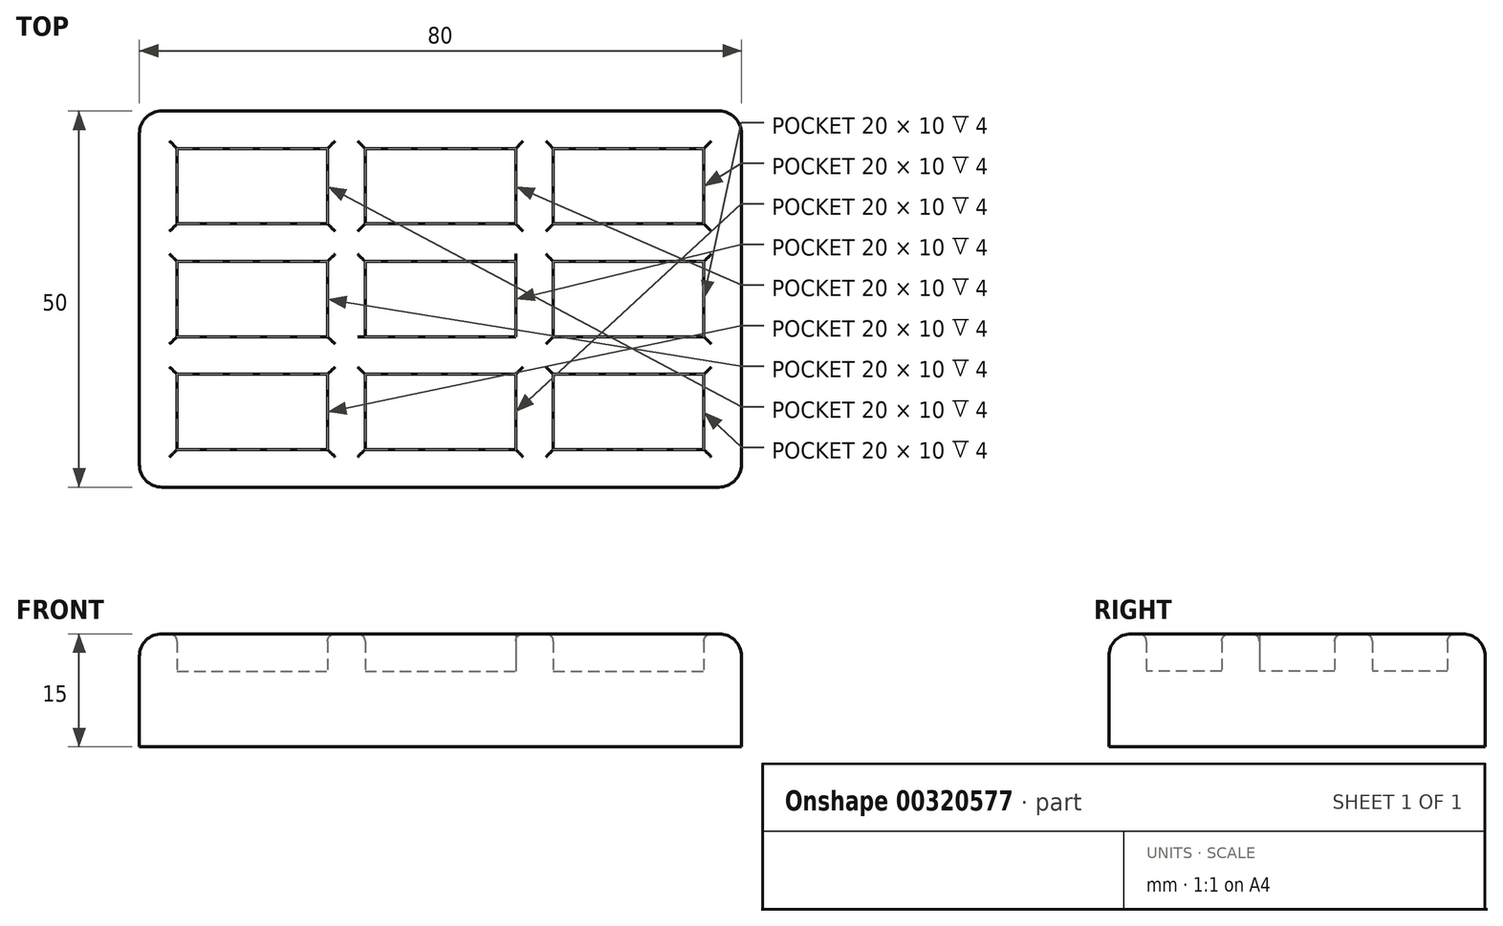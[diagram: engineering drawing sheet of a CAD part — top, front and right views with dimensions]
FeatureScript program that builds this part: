
annotation { "Feature Type Name" : "Feature", "Feature Type Description" : "" }
export const myFeature = defineFeature(function(context is Context, id is Id, definition is map)
    precondition{}
    {
        {
            var Q0;
            Q0=qCreatedBy(makeId("Top.planeOp"),FACE);
            var sketch = newSketch(context, id + "F0", { "sketchPlane" : qUnion([Q0])});
            skLineSegment(sketch, "E0.bottom", {"start": v(-40, 25) * mm, "end": v(40, 25) * mm});
            skLineSegment(sketch, "E0.top", {"start": v(-40, -25) * mm, "end": v(40, -25) * mm});
            skLineSegment(sketch, "E0.left", {"start": v(-40, 25) * mm, "end": v(-40, -25) * mm});
            skLineSegment(sketch, "E0.right", {"start": v(40, 25) * mm, "end": v(40, -25) * mm});
            skPoint(sketch, "E1", {"position": v(0, 25) * mm});
            skPoint(sketch, "E2", {"position": v(-40, 0) * mm});
            skLineSegment(sketch, "E3.bottom", {"start": v(-35, 20) * mm, "end": v(-15, 20) * mm});
            skLineSegment(sketch, "E3.top", {"start": v(-35, 10) * mm, "end": v(-15, 10) * mm});
            skLineSegment(sketch, "E3.left", {"start": v(-35, 20) * mm, "end": v(-35, 10) * mm});
            skLineSegment(sketch, "E3.right", {"start": v(-15, 20) * mm, "end": v(-15, 10) * mm});
            skLineSegment(sketch, "E4.0.1.0", {"start": v(-35, -5) * mm, "end": v(-15, -5) * mm});
            skLineSegment(sketch, "E4.0.1.1", {"start": v(-15, 5) * mm, "end": v(-15, -5) * mm});
            skLineSegment(sketch, "E4.0.1.2", {"start": v(-35, 5) * mm, "end": v(-15, 5) * mm});
            skLineSegment(sketch, "E4.0.1.3", {"start": v(-35, 5) * mm, "end": v(-35, -5) * mm});
            skLineSegment(sketch, "E4.0.2.0", {"start": v(-35, -20) * mm, "end": v(-15, -20) * mm});
            skLineSegment(sketch, "E4.0.2.1", {"start": v(-15, -10) * mm, "end": v(-15, -20) * mm});
            skLineSegment(sketch, "E4.0.2.2", {"start": v(-35, -10) * mm, "end": v(-15, -10) * mm});
            skLineSegment(sketch, "E4.0.2.3", {"start": v(-35, -10) * mm, "end": v(-35, -20) * mm});
            skLineSegment(sketch, "E4.1.0.0", {"start": v(-10, 10) * mm, "end": v(10, 10) * mm});
            skLineSegment(sketch, "E4.1.0.1", {"start": v(10, 20) * mm, "end": v(10, 10) * mm});
            skLineSegment(sketch, "E4.1.0.2", {"start": v(-10, 20) * mm, "end": v(10, 20) * mm});
            skLineSegment(sketch, "E4.1.0.3", {"start": v(-10, 20) * mm, "end": v(-10, 10) * mm});
            skLineSegment(sketch, "E4.1.1.0", {"start": v(-10, -5) * mm, "end": v(10, -5) * mm});
            skLineSegment(sketch, "E4.1.1.1", {"start": v(10, 5) * mm, "end": v(10, -5) * mm});
            skLineSegment(sketch, "E4.1.1.2", {"start": v(-10, 5) * mm, "end": v(10, 5) * mm});
            skLineSegment(sketch, "E4.1.1.3", {"start": v(-10, 5) * mm, "end": v(-10, -5) * mm});
            skLineSegment(sketch, "E4.1.2.0", {"start": v(-10, -20) * mm, "end": v(10, -20) * mm});
            skLineSegment(sketch, "E4.1.2.1", {"start": v(10, -10) * mm, "end": v(10, -20) * mm});
            skLineSegment(sketch, "E4.1.2.2", {"start": v(-10, -10) * mm, "end": v(10, -10) * mm});
            skLineSegment(sketch, "E4.1.2.3", {"start": v(-10, -10) * mm, "end": v(-10, -20) * mm});
            skLineSegment(sketch, "E4.2.0.0", {"start": v(15, 10) * mm, "end": v(35, 10) * mm});
            skLineSegment(sketch, "E4.2.0.1", {"start": v(35, 20) * mm, "end": v(35, 10) * mm});
            skLineSegment(sketch, "E4.2.0.2", {"start": v(15, 20) * mm, "end": v(35, 20) * mm});
            skLineSegment(sketch, "E4.2.0.3", {"start": v(15, 20) * mm, "end": v(15, 10) * mm});
            skLineSegment(sketch, "E4.2.1.0", {"start": v(15, -5) * mm, "end": v(35, -5) * mm});
            skLineSegment(sketch, "E4.2.1.1", {"start": v(35, 5) * mm, "end": v(35, -5) * mm});
            skLineSegment(sketch, "E4.2.1.2", {"start": v(15, 5) * mm, "end": v(35, 5) * mm});
            skLineSegment(sketch, "E4.2.1.3", {"start": v(15, 5) * mm, "end": v(15, -5) * mm});
            skLineSegment(sketch, "E4.2.2.0", {"start": v(15, -20) * mm, "end": v(35, -20) * mm});
            skLineSegment(sketch, "E4.2.2.1", {"start": v(35, -10) * mm, "end": v(35, -20) * mm});
            skLineSegment(sketch, "E4.2.2.2", {"start": v(15, -10) * mm, "end": v(35, -10) * mm});
            skLineSegment(sketch, "E4.2.2.3", {"start": v(15, -10) * mm, "end": v(15, -20) * mm});
            skLineSegment(sketch, "E4.direction1", {"start": v(-35, 10) * mm, "end": v(-10, 10) * mm, "construction": true});
            skLineSegment(sketch, "E4.direction2", {"start": v(-35, 10) * mm, "end": v(-35, -5) * mm, "construction": true});
            skSolve(sketch);
        }
        {
            var Q0;
            Q0=makeQuery(id+"F0.imprint","IMPRINT",FACE,{"disambiguationData":[TD([[makeQuery(id+"F0.imprint","IMPRINT",EDGE,{"derivedFrom":sQuery(id+"F0.wireOp",EDGE,"E0.bottom")}),-1.0]])]});
            var Q1;
            Q1=makeQuery(id+"F0.imprint","IMPRINT",FACE,{"disambiguationData":[TD([[makeQuery(id+"F0.imprint","IMPRINT",EDGE,{"derivedFrom":sQuery(id+"F0.wireOp",EDGE,"E3.bottom")}),-1.0]])]});
            var Q2;
            Q2=makeQuery(id+"F0.imprint","IMPRINT",FACE,{"disambiguationData":[TD([[makeQuery(id+"F0.imprint","IMPRINT",EDGE,{"derivedFrom":sQuery(id+"F0.wireOp",EDGE,"E4.1.0.0")}),1.0]])]});
            var Q3;
            Q3=makeQuery(id+"F0.imprint","IMPRINT",FACE,{"disambiguationData":[TD([[makeQuery(id+"F0.imprint","IMPRINT",EDGE,{"derivedFrom":sQuery(id+"F0.wireOp",EDGE,"E4.2.0.0")}),1.0]])]});
            var Q4;
            Q4=makeQuery(id+"F0.imprint","IMPRINT",FACE,{"disambiguationData":[TD([[makeQuery(id+"F0.imprint","IMPRINT",EDGE,{"derivedFrom":sQuery(id+"F0.wireOp",EDGE,"E4.2.1.0")}),1.0]])]});
            var Q5;
            Q5=makeQuery(id+"F0.imprint","IMPRINT",FACE,{"disambiguationData":[TD([[makeQuery(id+"F0.imprint","IMPRINT",EDGE,{"derivedFrom":sQuery(id+"F0.wireOp",EDGE,"E4.1.1.0")}),1.0]])]});
            var Q6;
            Q6=makeQuery(id+"F0.imprint","IMPRINT",FACE,{"disambiguationData":[TD([[makeQuery(id+"F0.imprint","IMPRINT",EDGE,{"derivedFrom":sQuery(id+"F0.wireOp",EDGE,"E4.0.1.0")}),1.0]])]});
            var Q7;
            Q7=makeQuery(id+"F0.imprint","IMPRINT",FACE,{"disambiguationData":[TD([[makeQuery(id+"F0.imprint","IMPRINT",EDGE,{"derivedFrom":sQuery(id+"F0.wireOp",EDGE,"E4.0.2.0")}),1.0]])]});
            var Q8;
            Q8=makeQuery(id+"F0.imprint","IMPRINT",FACE,{"disambiguationData":[TD([[makeQuery(id+"F0.imprint","IMPRINT",EDGE,{"derivedFrom":sQuery(id+"F0.wireOp",EDGE,"E4.1.2.0")}),1.0]])]});
            var Q9;
            Q9=makeQuery(id+"F0.imprint","IMPRINT",FACE,{"disambiguationData":[TD([[makeQuery(id+"F0.imprint","IMPRINT",EDGE,{"derivedFrom":sQuery(id+"F0.wireOp",EDGE,"E4.2.2.0")}),1.0]])]});
            extrude(context, id + "F1", {"entities" : qUnion([Q0, Q1, Q2, Q3, Q4, Q5, Q6, Q7, Q8, Q9]), "oppositeDirection" : true, "depth" : 10 * mm});
        }
        {
            var Q0;
            Q0 = qSketchRegion(id + "F0", true);
            extrude(context, id + "F2", {"entities" : qUnion([Q0]), "operationType" : NewBodyOperationType.ADD, "depth" : 5 * mm});
        }
        {
            var Q0;
            {var subQ0=sQuery(id+"F0.wireOp",EDGE,"E0.left");var subQ1=sQuery(id+"F0.wireOp",EDGE,"E0.top");Q0=makeQuery(id+"F2.boolean.opBoolean","MERGE",EDGE,{"derivedFrom":[makeQuery(id+"F1.opExtrude","SWEPT_EDGE",EDGE,{"disambiguationData":[OSD([subQ1,subQ0])]}),makeQuery(id+"F2.opExtrude","SWEPT_EDGE",EDGE,{"disambiguationData":[OSD([subQ1,subQ0])]})]});}
            var Q1;
            {var subQ0=sQuery(id+"F0.wireOp",EDGE,"E0.right");var subQ1=sQuery(id+"F0.wireOp",EDGE,"E0.top");Q1=makeQuery(id+"F2.boolean.opBoolean","MERGE",EDGE,{"derivedFrom":[makeQuery(id+"F1.opExtrude","SWEPT_EDGE",EDGE,{"disambiguationData":[OSD([subQ1,subQ0])]}),makeQuery(id+"F2.opExtrude","SWEPT_EDGE",EDGE,{"disambiguationData":[OSD([subQ1,subQ0])]})]});}
            var Q2;
            Q2=makeQuery(id+"F2.opExtrude","CAP_EDGE",EDGE,{"disambiguationData":[OSD([sQuery(id+"F0.wireOp",EDGE,"E0.top")])],"isStart":false});
            var Q3;
            Q3=makeQuery(id+"F2.opExtrude","CAP_EDGE",EDGE,{"disambiguationData":[OSD([sQuery(id+"F0.wireOp",EDGE,"E0.left")])],"isStart":false});
            var Q4;
            Q4=makeQuery(id+"F2.opExtrude","CAP_EDGE",EDGE,{"disambiguationData":[OSD([sQuery(id+"F0.wireOp",EDGE,"E0.right")])],"isStart":false});
            var Q5;
            {var subQ0=sQuery(id+"F0.wireOp",EDGE,"E0.right");var subQ1=sQuery(id+"F0.wireOp",EDGE,"E0.bottom");Q5=makeQuery(id+"F2.boolean.opBoolean","MERGE",EDGE,{"derivedFrom":[makeQuery(id+"F1.opExtrude","SWEPT_EDGE",EDGE,{"disambiguationData":[OSD([subQ1,subQ0])]}),makeQuery(id+"F2.opExtrude","SWEPT_EDGE",EDGE,{"disambiguationData":[OSD([subQ1,subQ0])]})]});}
            var Q6;
            Q6=makeQuery(id+"F2.opExtrude","CAP_EDGE",EDGE,{"disambiguationData":[OSD([sQuery(id+"F0.wireOp",EDGE,"E0.bottom")])],"isStart":false});
            var Q7;
            {var subQ0=sQuery(id+"F0.wireOp",EDGE,"E0.left");var subQ1=sQuery(id+"F0.wireOp",EDGE,"E0.bottom");Q7=makeQuery(id+"F2.boolean.opBoolean","MERGE",EDGE,{"derivedFrom":[makeQuery(id+"F1.opExtrude","SWEPT_EDGE",EDGE,{"disambiguationData":[OSD([subQ1,subQ0])]}),makeQuery(id+"F2.opExtrude","SWEPT_EDGE",EDGE,{"disambiguationData":[OSD([subQ1,subQ0])]})]});}
            fillet(context, id + "F3", {"entities" : qUnion([Q0, Q1, Q2, Q3, Q4, Q5, Q6, Q7]), "radius" : 3 * mm, "tangentPropagation" : true, "allowEdgeOverflow" : false});
        }
        {
            var Q0;
            Q0=makeQuery(id+"F2.opExtrude","CAP_EDGE",EDGE,{"disambiguationData":[OSD([sQuery(id+"F0.wireOp",EDGE,"E4.0.2.1")])],"isStart":false});
            var Q1;
            Q1=makeQuery(id+"F2.opExtrude","CAP_EDGE",EDGE,{"disambiguationData":[OSD([sQuery(id+"F0.wireOp",EDGE,"E4.0.2.2")])],"isStart":false});
            var Q2;
            Q2=makeQuery(id+"F2.opExtrude","CAP_EDGE",EDGE,{"disambiguationData":[OSD([sQuery(id+"F0.wireOp",EDGE,"E4.0.2.3")])],"isStart":false});
            var Q3;
            Q3=makeQuery(id+"F2.opExtrude","CAP_EDGE",EDGE,{"disambiguationData":[OSD([sQuery(id+"F0.wireOp",EDGE,"E4.0.2.0")])],"isStart":false});
            var Q4;
            Q4=makeQuery(id+"F2.opExtrude","CAP_EDGE",EDGE,{"disambiguationData":[OSD([sQuery(id+"F0.wireOp",EDGE,"E4.0.1.1")])],"isStart":false});
            var Q5;
            Q5=makeQuery(id+"F2.opExtrude","CAP_EDGE",EDGE,{"disambiguationData":[OSD([sQuery(id+"F0.wireOp",EDGE,"E4.0.1.0")])],"isStart":false});
            var Q6;
            Q6=makeQuery(id+"F2.opExtrude","CAP_EDGE",EDGE,{"disambiguationData":[OSD([sQuery(id+"F0.wireOp",EDGE,"E4.0.1.3")])],"isStart":false});
            var Q7;
            Q7=makeQuery(id+"F2.opExtrude","CAP_EDGE",EDGE,{"disambiguationData":[OSD([sQuery(id+"F0.wireOp",EDGE,"E4.0.1.2")])],"isStart":false});
            var Q8;
            Q8=makeQuery(id+"F2.opExtrude","CAP_EDGE",EDGE,{"disambiguationData":[OSD([sQuery(id+"F0.wireOp",EDGE,"E3.bottom")])],"isStart":false});
            var Q9;
            Q9=makeQuery(id+"F2.opExtrude","CAP_EDGE",EDGE,{"disambiguationData":[OSD([sQuery(id+"F0.wireOp",EDGE,"E3.right")])],"isStart":false});
            var Q10;
            Q10=makeQuery(id+"F2.opExtrude","CAP_EDGE",EDGE,{"disambiguationData":[OSD([sQuery(id+"F0.wireOp",EDGE,"E3.top")])],"isStart":false});
            var Q11;
            Q11=makeQuery(id+"F2.opExtrude","CAP_EDGE",EDGE,{"disambiguationData":[OSD([sQuery(id+"F0.wireOp",EDGE,"E3.left")])],"isStart":false});
            var Q12;
            Q12=makeQuery(id+"F2.opExtrude","CAP_EDGE",EDGE,{"disambiguationData":[OSD([sQuery(id+"F0.wireOp",EDGE,"E4.1.0.3")])],"isStart":false});
            var Q13;
            Q13=makeQuery(id+"F2.opExtrude","CAP_EDGE",EDGE,{"disambiguationData":[OSD([sQuery(id+"F0.wireOp",EDGE,"E4.1.0.2")])],"isStart":false});
            var Q14;
            Q14=makeQuery(id+"F2.opExtrude","CAP_EDGE",EDGE,{"disambiguationData":[OSD([sQuery(id+"F0.wireOp",EDGE,"E4.1.0.0")])],"isStart":false});
            var Q15;
            Q15=makeQuery(id+"F2.opExtrude","CAP_EDGE",EDGE,{"disambiguationData":[OSD([sQuery(id+"F0.wireOp",EDGE,"E4.1.0.1")])],"isStart":false});
            var Q16;
            Q16=makeQuery(id+"F2.opExtrude","CAP_EDGE",EDGE,{"disambiguationData":[OSD([sQuery(id+"F0.wireOp",EDGE,"E4.1.1.2")])],"isStart":false});
            var Q17;
            Q17=makeQuery(id+"F2.opExtrude","CAP_EDGE",EDGE,{"disambiguationData":[OSD([sQuery(id+"F0.wireOp",EDGE,"E4.1.1.3")])],"isStart":false});
            var Q18;
            Q18=makeQuery(id+"F2.opExtrude","CAP_EDGE",EDGE,{"disambiguationData":[OSD([sQuery(id+"F0.wireOp",EDGE,"E4.1.2.3")])],"isStart":false});
            var Q19;
            Q19=makeQuery(id+"F2.opExtrude","CAP_EDGE",EDGE,{"disambiguationData":[OSD([sQuery(id+"F0.wireOp",EDGE,"E4.1.2.2")])],"isStart":false});
            var Q20;
            Q20=makeQuery(id+"F2.opExtrude","CAP_EDGE",EDGE,{"disambiguationData":[OSD([sQuery(id+"F0.wireOp",EDGE,"E4.1.2.0")])],"isStart":false});
            var Q21;
            Q21=makeQuery(id+"F2.opExtrude","CAP_EDGE",EDGE,{"disambiguationData":[OSD([sQuery(id+"F0.wireOp",EDGE,"E4.1.2.1")])],"isStart":false});
            var Q22;
            Q22=makeQuery(id+"F2.opExtrude","CAP_EDGE",EDGE,{"disambiguationData":[OSD([sQuery(id+"F0.wireOp",EDGE,"E4.2.1.3")])],"isStart":false});
            var Q23;
            Q23=makeQuery(id+"F2.opExtrude","CAP_EDGE",EDGE,{"disambiguationData":[OSD([sQuery(id+"F0.wireOp",EDGE,"E4.2.1.2")])],"isStart":false});
            var Q24;
            Q24=makeQuery(id+"F2.opExtrude","CAP_EDGE",EDGE,{"disambiguationData":[OSD([sQuery(id+"F0.wireOp",EDGE,"E4.2.0.3")])],"isStart":false});
            var Q25;
            Q25=makeQuery(id+"F2.opExtrude","CAP_EDGE",EDGE,{"disambiguationData":[OSD([sQuery(id+"F0.wireOp",EDGE,"E4.2.0.2")])],"isStart":false});
            var Q26;
            Q26=makeQuery(id+"F2.opExtrude","CAP_EDGE",EDGE,{"disambiguationData":[OSD([sQuery(id+"F0.wireOp",EDGE,"E4.2.1.0")])],"isStart":false});
            var Q27;
            Q27=makeQuery(id+"F2.opExtrude","CAP_EDGE",EDGE,{"disambiguationData":[OSD([sQuery(id+"F0.wireOp",EDGE,"E4.2.2.3")])],"isStart":false});
            var Q28;
            Q28=makeQuery(id+"F2.opExtrude","CAP_EDGE",EDGE,{"disambiguationData":[OSD([sQuery(id+"F0.wireOp",EDGE,"E4.2.2.2")])],"isStart":false});
            var Q29;
            Q29=makeQuery(id+"F2.opExtrude","CAP_EDGE",EDGE,{"disambiguationData":[OSD([sQuery(id+"F0.wireOp",EDGE,"E4.2.2.0")])],"isStart":false});
            var Q30;
            Q30=makeQuery(id+"F2.opExtrude","CAP_EDGE",EDGE,{"disambiguationData":[OSD([sQuery(id+"F0.wireOp",EDGE,"E4.2.2.1")])],"isStart":false});
            var Q31;
            Q31=makeQuery(id+"F2.opExtrude","CAP_EDGE",EDGE,{"disambiguationData":[OSD([sQuery(id+"F0.wireOp",EDGE,"E4.2.1.1")])],"isStart":false});
            var Q32;
            Q32=makeQuery(id+"F2.opExtrude","CAP_EDGE",EDGE,{"disambiguationData":[OSD([sQuery(id+"F0.wireOp",EDGE,"E4.2.0.1")])],"isStart":false});
            var Q33;
            Q33=makeQuery(id+"F2.opExtrude","CAP_EDGE",EDGE,{"disambiguationData":[OSD([sQuery(id+"F0.wireOp",EDGE,"E4.2.0.0")])],"isStart":false});
            fillet(context, id + "F4", {"entities" : qUnion([Q0, Q1, Q2, Q3, Q4, Q5, Q6, Q7, Q8, Q9, Q10, Q11, Q12, Q13, Q14, Q15, Q16, Q17, Q18, Q19, Q20, Q21, Q22, Q23, Q24, Q25, Q26, Q27, Q28, Q29, Q30, Q31, Q32, Q33]), "radius" : 1 * mm, "tangentPropagation" : true, "allowEdgeOverflow" : false});
        }
    });
